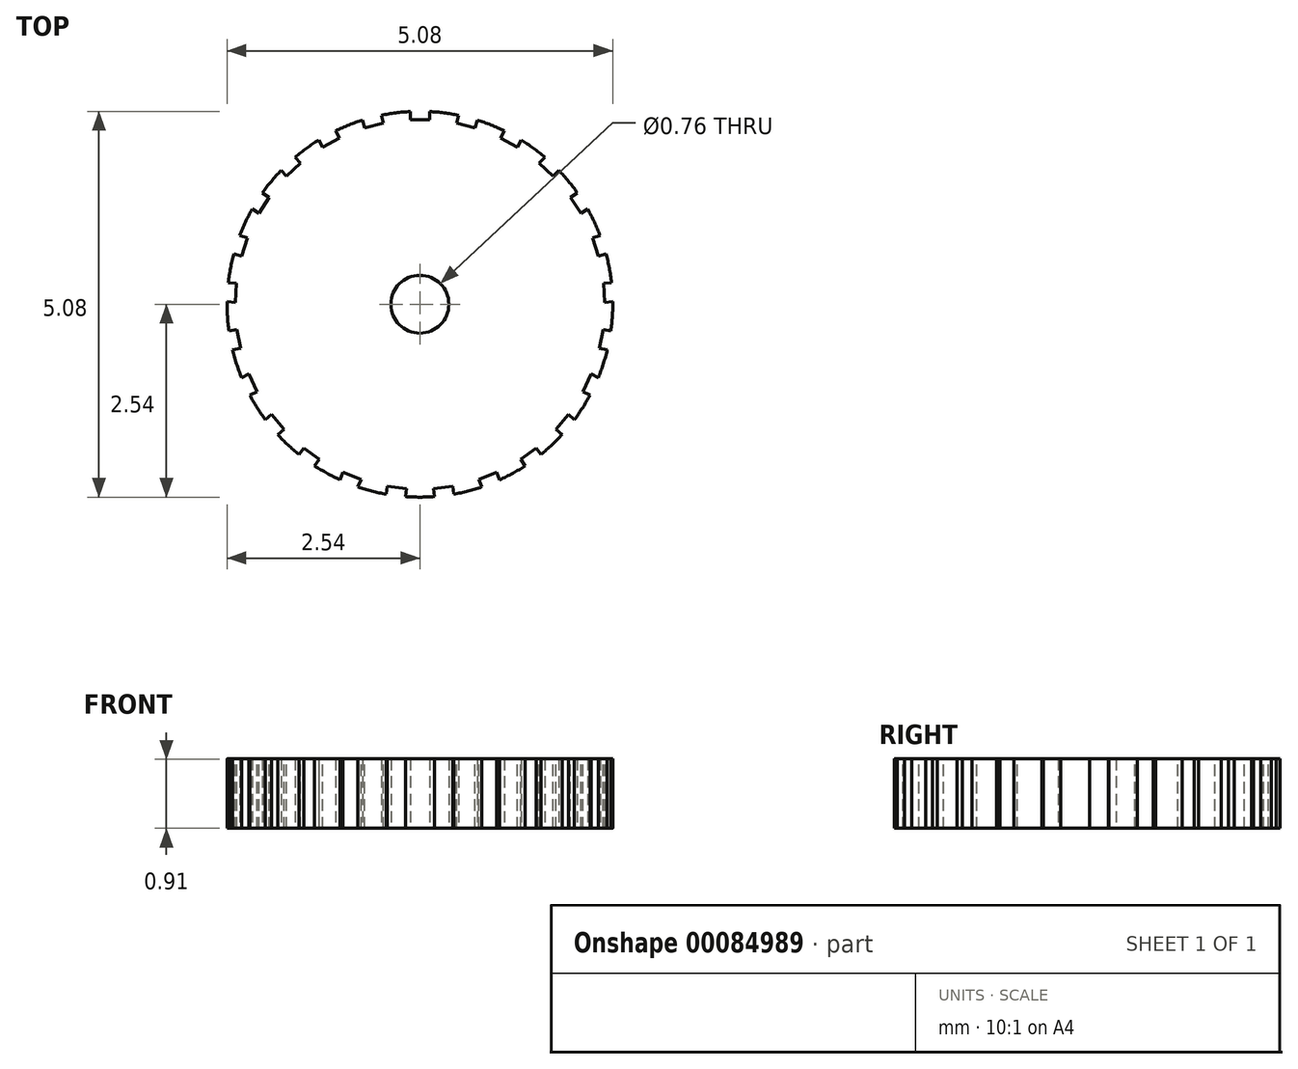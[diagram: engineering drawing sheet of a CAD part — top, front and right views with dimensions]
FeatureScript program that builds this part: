
annotation { "Feature Type Name" : "Feature", "Feature Type Description" : "" }
export const myFeature = defineFeature(function(context is Context, id is Id, definition is map)
    precondition{}
    {
        {
            var Q0;
            Q0=qCreatedBy(makeId("Top.planeOp"),FACE);
            var sketch = newSketch(context, id + "F0", { "sketchPlane" : qUnion([Q0])});
            skCircle(sketch, "E0", {"center": v(0, 0) * mm, "radius": 2.54 * mm});
            skCircle(sketch, "E1", {"center": v(0, 0) * mm, "radius": 0.38 * mm});
            skSolve(sketch);
        }
        {
            var Q0;
            Q0 = qSketchRegion(id + "F0", true);
            extrude(context, id + "F1", {"entities" : qUnion([Q0]), "depth" : 0.91 * mm});
        }
        {
            var Q0;
            Q0=makeQuery(id+"F1.opExtrude","CAP_FACE",FACE,{"disambiguationData":[OSD([sQuery(id+"F0.wireOp",EDGE,"E0"),sQuery(id+"F0.wireOp",EDGE,"E1")])],"isStart":false});
            var sketch = newSketch(context, id + "F2", { "sketchPlane" : qUnion([Q0])});
            skLineSegment(sketch, "E2.bottom", {"start": v(-0.13, 2.67) * mm, "end": v(0.13, 2.67) * mm});
            skLineSegment(sketch, "E2.top", {"start": v(-0.13, 2.43) * mm, "end": v(0.13, 2.43) * mm});
            skLineSegment(sketch, "E2.left", {"start": v(-0.13, 2.67) * mm, "end": v(-0.13, 2.43) * mm});
            skLineSegment(sketch, "E2.right", {"start": v(0.13, 2.67) * mm, "end": v(0.13, 2.43) * mm});
            skLineSegment(sketch, "E3.1.0", {"start": v(-0.54, 2.62) * mm, "end": v(-0.48, 2.39) * mm});
            skLineSegment(sketch, "E3.1.1", {"start": v(-0.79, 2.55) * mm, "end": v(-0.54, 2.62) * mm});
            skLineSegment(sketch, "E3.1.2", {"start": v(-0.79, 2.55) * mm, "end": v(-0.73, 2.32) * mm});
            skLineSegment(sketch, "E3.1.3", {"start": v(-0.73, 2.32) * mm, "end": v(-0.48, 2.39) * mm});
            skLineSegment(sketch, "E3.2.0", {"start": v(-1.17, 2.4) * mm, "end": v(-1.06, 2.2) * mm});
            skLineSegment(sketch, "E3.2.1", {"start": v(-1.4, 2.28) * mm, "end": v(-1.17, 2.4) * mm});
            skLineSegment(sketch, "E3.2.2", {"start": v(-1.4, 2.28) * mm, "end": v(-1.28, 2.07) * mm});
            skLineSegment(sketch, "E3.2.3", {"start": v(-1.28, 2.07) * mm, "end": v(-1.06, 2.2) * mm});
            skLineSegment(sketch, "E3.3.0", {"start": v(-1.73, 2.03) * mm, "end": v(-1.57, 1.86) * mm});
            skLineSegment(sketch, "E3.3.1", {"start": v(-1.92, 1.86) * mm, "end": v(-1.73, 2.03) * mm});
            skLineSegment(sketch, "E3.3.2", {"start": v(-1.92, 1.86) * mm, "end": v(-1.76, 1.68) * mm});
            skLineSegment(sketch, "E3.3.3", {"start": v(-1.76, 1.68) * mm, "end": v(-1.57, 1.86) * mm});
            skLineSegment(sketch, "E3.4.0", {"start": v(-2.18, 1.54) * mm, "end": v(-1.98, 1.4) * mm});
            skLineSegment(sketch, "E3.4.1", {"start": v(-2.32, 1.32) * mm, "end": v(-2.18, 1.54) * mm});
            skLineSegment(sketch, "E3.4.2", {"start": v(-2.32, 1.32) * mm, "end": v(-2.12, 1.2) * mm});
            skLineSegment(sketch, "E3.4.3", {"start": v(-2.12, 1.2) * mm, "end": v(-1.98, 1.4) * mm});
            skLineSegment(sketch, "E3.5.0", {"start": v(-2.5, 0.95) * mm, "end": v(-2.27, 0.87) * mm});
            skLineSegment(sketch, "E3.5.1", {"start": v(-2.58, 0.7) * mm, "end": v(-2.5, 0.95) * mm});
            skLineSegment(sketch, "E3.5.2", {"start": v(-2.58, 0.7) * mm, "end": v(-2.35, 0.63) * mm});
            skLineSegment(sketch, "E3.5.3", {"start": v(-2.35, 0.63) * mm, "end": v(-2.27, 0.87) * mm});
            skLineSegment(sketch, "E3.6.0", {"start": v(-2.65, 0.3) * mm, "end": v(-2.42, 0.28) * mm});
            skLineSegment(sketch, "E3.6.1", {"start": v(-2.67, 0.04) * mm, "end": v(-2.65, 0.3) * mm});
            skLineSegment(sketch, "E3.6.2", {"start": v(-2.67, 0.04) * mm, "end": v(-2.43, 0.03) * mm});
            skLineSegment(sketch, "E3.6.3", {"start": v(-2.43, 0.03) * mm, "end": v(-2.42, 0.28) * mm});
            skLineSegment(sketch, "E3.7.0", {"start": v(-2.64, -0.38) * mm, "end": v(-2.41, -0.33) * mm});
            skLineSegment(sketch, "E3.7.1", {"start": v(-2.6, -0.62) * mm, "end": v(-2.64, -0.38) * mm});
            skLineSegment(sketch, "E3.7.2", {"start": v(-2.6, -0.62) * mm, "end": v(-2.36, -0.58) * mm});
            skLineSegment(sketch, "E3.7.3", {"start": v(-2.36, -0.58) * mm, "end": v(-2.41, -0.33) * mm});
            skLineSegment(sketch, "E3.8.0", {"start": v(-2.47, -1.02) * mm, "end": v(-2.25, -0.92) * mm});
            skLineSegment(sketch, "E3.8.1", {"start": v(-2.36, -1.25) * mm, "end": v(-2.47, -1.02) * mm});
            skLineSegment(sketch, "E3.8.2", {"start": v(-2.36, -1.25) * mm, "end": v(-2.15, -1.15) * mm});
            skLineSegment(sketch, "E3.8.3", {"start": v(-2.15, -1.15) * mm, "end": v(-2.25, -0.92) * mm});
            skLineSegment(sketch, "E3.9.0", {"start": v(-2.14, -1.6) * mm, "end": v(-1.95, -1.45) * mm});
            skLineSegment(sketch, "E3.9.1", {"start": v(-1.97, -1.8) * mm, "end": v(-2.14, -1.6) * mm});
            skLineSegment(sketch, "E3.9.2", {"start": v(-1.97, -1.8) * mm, "end": v(-1.8, -1.65) * mm});
            skLineSegment(sketch, "E3.9.3", {"start": v(-1.8, -1.65) * mm, "end": v(-1.95, -1.45) * mm});
            skLineSegment(sketch, "E3.10.0", {"start": v(-1.67, -2.08) * mm, "end": v(-1.53, -1.9) * mm});
            skLineSegment(sketch, "E3.10.1", {"start": v(-1.47, -2.23) * mm, "end": v(-1.67, -2.08) * mm});
            skLineSegment(sketch, "E3.10.2", {"start": v(-1.47, -2.23) * mm, "end": v(-1.33, -2.04) * mm});
            skLineSegment(sketch, "E3.10.3", {"start": v(-1.33, -2.04) * mm, "end": v(-1.53, -1.9) * mm});
            skLineSegment(sketch, "E3.11.0", {"start": v(-1.1, -2.43) * mm, "end": v(-1.01, -2.21) * mm});
            skLineSegment(sketch, "E3.11.1", {"start": v(-0.86, -2.53) * mm, "end": v(-1.1, -2.43) * mm});
            skLineSegment(sketch, "E3.11.2", {"start": v(-0.86, -2.53) * mm, "end": v(-0.78, -2.3) * mm});
            skLineSegment(sketch, "E3.11.3", {"start": v(-0.78, -2.3) * mm, "end": v(-1.01, -2.21) * mm});
            skLineSegment(sketch, "E3.12.0", {"start": v(-0.46, -2.63) * mm, "end": v(-0.43, -2.4) * mm});
            skLineSegment(sketch, "E3.12.1", {"start": v(-0.2, -2.66) * mm, "end": v(-0.46, -2.63) * mm});
            skLineSegment(sketch, "E3.12.2", {"start": v(-0.2, -2.66) * mm, "end": v(-0.18, -2.43) * mm});
            skLineSegment(sketch, "E3.12.3", {"start": v(-0.18, -2.43) * mm, "end": v(-0.43, -2.4) * mm});
            skLineSegment(sketch, "E3.13.0", {"start": v(0.2, -2.66) * mm, "end": v(0.18, -2.43) * mm});
            skLineSegment(sketch, "E3.13.1", {"start": v(0.46, -2.63) * mm, "end": v(0.2, -2.66) * mm});
            skLineSegment(sketch, "E3.13.2", {"start": v(0.46, -2.63) * mm, "end": v(0.43, -2.4) * mm});
            skLineSegment(sketch, "E3.13.3", {"start": v(0.43, -2.4) * mm, "end": v(0.18, -2.43) * mm});
            skLineSegment(sketch, "E3.14.0", {"start": v(0.86, -2.53) * mm, "end": v(0.78, -2.3) * mm});
            skLineSegment(sketch, "E3.14.1", {"start": v(1.1, -2.43) * mm, "end": v(0.86, -2.53) * mm});
            skLineSegment(sketch, "E3.14.2", {"start": v(1.1, -2.43) * mm, "end": v(1.01, -2.21) * mm});
            skLineSegment(sketch, "E3.14.3", {"start": v(1.01, -2.21) * mm, "end": v(0.78, -2.3) * mm});
            skLineSegment(sketch, "E3.15.0", {"start": v(1.47, -2.23) * mm, "end": v(1.33, -2.04) * mm});
            skLineSegment(sketch, "E3.15.1", {"start": v(1.67, -2.08) * mm, "end": v(1.47, -2.23) * mm});
            skLineSegment(sketch, "E3.15.2", {"start": v(1.67, -2.08) * mm, "end": v(1.53, -1.9) * mm});
            skLineSegment(sketch, "E3.15.3", {"start": v(1.53, -1.9) * mm, "end": v(1.33, -2.04) * mm});
            skLineSegment(sketch, "E3.16.0", {"start": v(1.97, -1.8) * mm, "end": v(1.8, -1.65) * mm});
            skLineSegment(sketch, "E3.16.1", {"start": v(2.14, -1.6) * mm, "end": v(1.97, -1.8) * mm});
            skLineSegment(sketch, "E3.16.2", {"start": v(2.14, -1.6) * mm, "end": v(1.95, -1.45) * mm});
            skLineSegment(sketch, "E3.16.3", {"start": v(1.95, -1.45) * mm, "end": v(1.8, -1.65) * mm});
            skLineSegment(sketch, "E3.17.0", {"start": v(2.36, -1.25) * mm, "end": v(2.15, -1.15) * mm});
            skLineSegment(sketch, "E3.17.1", {"start": v(2.47, -1.02) * mm, "end": v(2.36, -1.25) * mm});
            skLineSegment(sketch, "E3.17.2", {"start": v(2.47, -1.02) * mm, "end": v(2.25, -0.92) * mm});
            skLineSegment(sketch, "E3.17.3", {"start": v(2.25, -0.92) * mm, "end": v(2.15, -1.15) * mm});
            skLineSegment(sketch, "E3.18.0", {"start": v(2.6, -0.62) * mm, "end": v(2.36, -0.58) * mm});
            skLineSegment(sketch, "E3.18.1", {"start": v(2.64, -0.38) * mm, "end": v(2.6, -0.62) * mm});
            skLineSegment(sketch, "E3.18.2", {"start": v(2.64, -0.38) * mm, "end": v(2.41, -0.33) * mm});
            skLineSegment(sketch, "E3.18.3", {"start": v(2.41, -0.33) * mm, "end": v(2.36, -0.58) * mm});
            skLineSegment(sketch, "E3.19.0", {"start": v(2.67, 0.04) * mm, "end": v(2.43, 0.03) * mm});
            skLineSegment(sketch, "E3.19.1", {"start": v(2.65, 0.3) * mm, "end": v(2.67, 0.04) * mm});
            skLineSegment(sketch, "E3.19.2", {"start": v(2.65, 0.3) * mm, "end": v(2.42, 0.28) * mm});
            skLineSegment(sketch, "E3.19.3", {"start": v(2.42, 0.28) * mm, "end": v(2.43, 0.03) * mm});
            skLineSegment(sketch, "E3.20.0", {"start": v(2.58, 0.7) * mm, "end": v(2.35, 0.63) * mm});
            skLineSegment(sketch, "E3.20.1", {"start": v(2.5, 0.95) * mm, "end": v(2.58, 0.7) * mm});
            skLineSegment(sketch, "E3.20.2", {"start": v(2.5, 0.95) * mm, "end": v(2.27, 0.87) * mm});
            skLineSegment(sketch, "E3.20.3", {"start": v(2.27, 0.87) * mm, "end": v(2.35, 0.63) * mm});
            skLineSegment(sketch, "E3.21.0", {"start": v(2.32, 1.32) * mm, "end": v(2.12, 1.2) * mm});
            skLineSegment(sketch, "E3.21.1", {"start": v(2.18, 1.54) * mm, "end": v(2.32, 1.32) * mm});
            skLineSegment(sketch, "E3.21.2", {"start": v(2.18, 1.54) * mm, "end": v(1.98, 1.4) * mm});
            skLineSegment(sketch, "E3.21.3", {"start": v(1.98, 1.4) * mm, "end": v(2.12, 1.2) * mm});
            skLineSegment(sketch, "E3.22.0", {"start": v(1.92, 1.86) * mm, "end": v(1.76, 1.68) * mm});
            skLineSegment(sketch, "E3.22.1", {"start": v(1.73, 2.03) * mm, "end": v(1.92, 1.86) * mm});
            skLineSegment(sketch, "E3.22.2", {"start": v(1.73, 2.03) * mm, "end": v(1.57, 1.86) * mm});
            skLineSegment(sketch, "E3.22.3", {"start": v(1.57, 1.86) * mm, "end": v(1.76, 1.68) * mm});
            skLineSegment(sketch, "E3.23.0", {"start": v(1.4, 2.28) * mm, "end": v(1.28, 2.07) * mm});
            skLineSegment(sketch, "E3.23.1", {"start": v(1.17, 2.4) * mm, "end": v(1.4, 2.28) * mm});
            skLineSegment(sketch, "E3.23.2", {"start": v(1.17, 2.4) * mm, "end": v(1.06, 2.2) * mm});
            skLineSegment(sketch, "E3.23.3", {"start": v(1.06, 2.2) * mm, "end": v(1.28, 2.07) * mm});
            skLineSegment(sketch, "E3.24.0", {"start": v(0.79, 2.55) * mm, "end": v(0.73, 2.32) * mm});
            skLineSegment(sketch, "E3.24.1", {"start": v(0.54, 2.62) * mm, "end": v(0.79, 2.55) * mm});
            skLineSegment(sketch, "E3.24.2", {"start": v(0.54, 2.62) * mm, "end": v(0.48, 2.39) * mm});
            skLineSegment(sketch, "E3.24.3", {"start": v(0.48, 2.39) * mm, "end": v(0.73, 2.32) * mm});
            skPoint(sketch, "E3.center", {"position": v(0, 0) * mm});
            skSolve(sketch);
        }
        {
            var Q0;
            Q0 = qSketchRegion(id + "F2", true);
            extrude(context, id + "F3", {"entities" : qUnion([Q0]), "operationType" : NewBodyOperationType.REMOVE, "oppositeDirection" : true, "depth" : 25.4 * mm});
        }
    });
